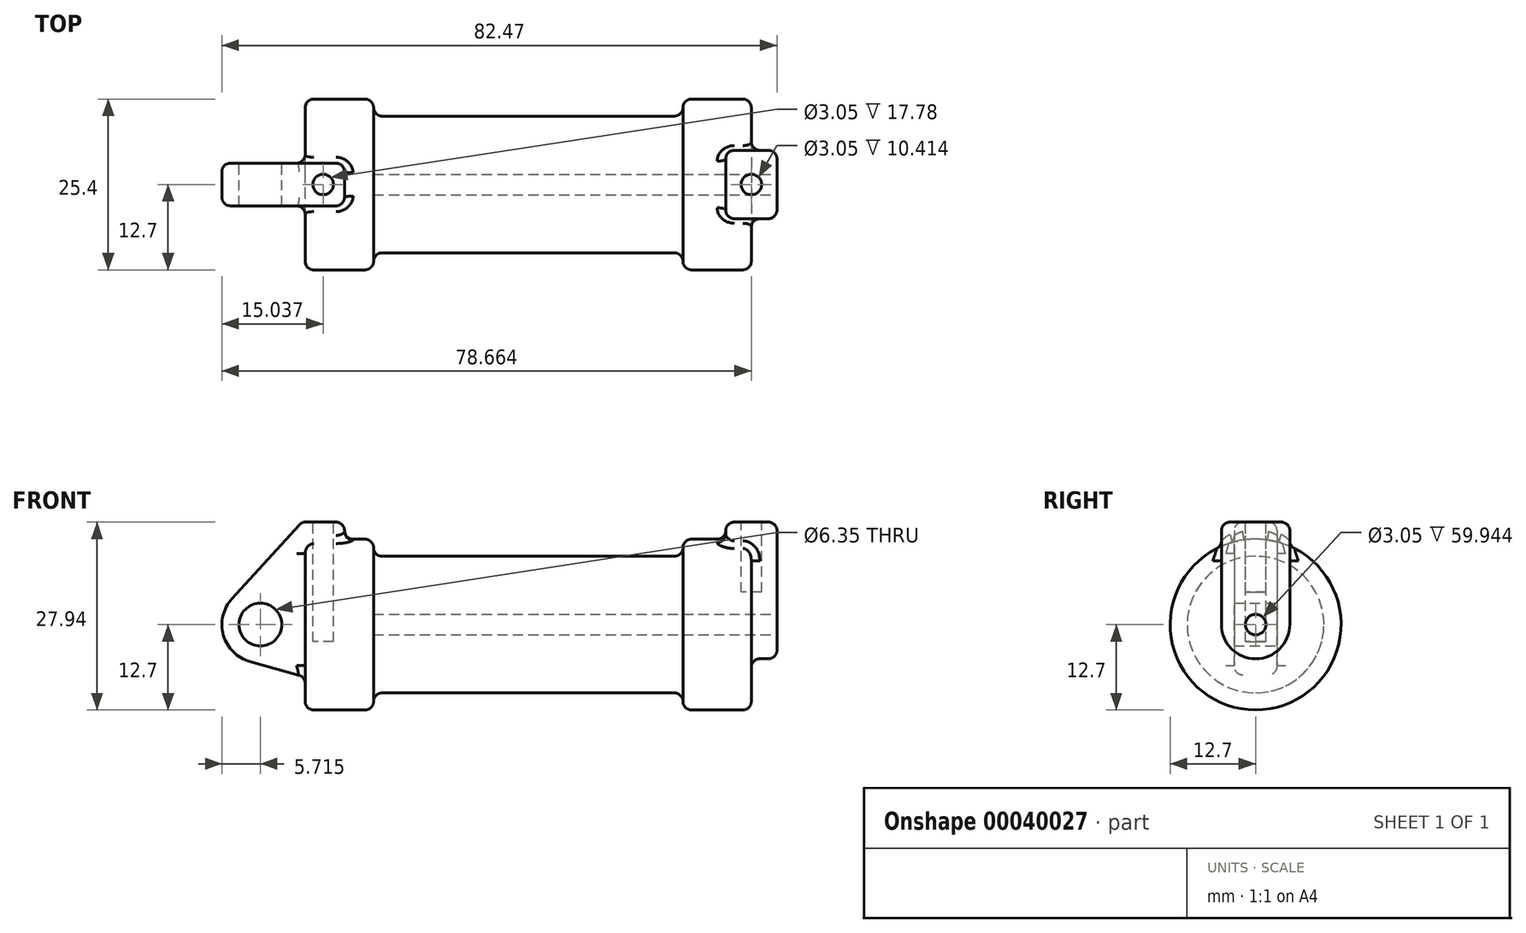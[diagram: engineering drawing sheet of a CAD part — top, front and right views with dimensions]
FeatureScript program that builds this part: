
annotation { "Feature Type Name" : "Feature", "Feature Type Description" : "" }
export const myFeature = defineFeature(function(context is Context, id is Id, definition is map)
    precondition{}
    {
        {
            var Q0;
            Q0=qCreatedBy(makeId("Front.planeOp"),FACE);
            var sketch = newSketch(context, id + "F0", { "sketchPlane" : qUnion([Q0])});
            skLineSegment(sketch, "E0", {"start": v(0, 0) * mm, "end": v(0, 12.7) * mm});
            skLineSegment(sketch, "E1", {"start": v(0, 12.7) * mm, "end": v(10.16, 12.7) * mm});
            skLineSegment(sketch, "E2", {"start": v(10.16, 12.7) * mm, "end": v(10.16, 10.16) * mm});
            skLineSegment(sketch, "E3", {"start": v(10.16, 10.16) * mm, "end": v(56.13, 10.16) * mm});
            skLineSegment(sketch, "E4", {"start": v(56.13, 10.16) * mm, "end": v(56.13, 12.7) * mm});
            skLineSegment(sketch, "E5", {"start": v(56.13, 12.7) * mm, "end": v(66.3, 12.7) * mm});
            skLineSegment(sketch, "E6", {"start": v(66.3, 12.7) * mm, "end": v(66.3, 0) * mm});
            skLineSegment(sketch, "E7", {"start": v(66.3, 0) * mm, "end": v(0, 0) * mm});
            skLineSegment(sketch, "E8", {"start": v(5.84, 15.24) * mm, "end": v(-0.5, 15.24) * mm});
            skLineSegment(sketch, "E9", {"start": v(-0.5, 15.24) * mm, "end": v(-10.88, 3.85) * mm});
            skLineSegment(sketch, "E10", {"start": v(0, 0) * mm, "end": v(-6.65, 0) * mm});
            skCircle(sketch, "E11", {"center": v(-6.65, 0) * mm, "radius": 5.72 * mm});
            skCircle(sketch, "E12", {"center": v(-6.65, 0) * mm, "radius": 3.18 * mm});
            skLineSegment(sketch, "E13", {"start": v(5.84, 15.24) * mm, "end": v(5.84, -9.4) * mm});
            skLineSegment(sketch, "E14", {"start": v(5.84, -9.4) * mm, "end": v(-8.18, -5.5) * mm});
            skSolve(sketch);
        }
        {
            var Q0;
            {var subQ6=sQuery(id+"F0.wireOp",EDGE,"E2");Q0=makeQuery(id+"F0.imprint","IMPRINT",FACE,{"disambiguationData":[TD([[makeQuery(id+"F0.imprint","IMPRINT",EDGE,{"derivedFrom":subQ6}),-1.0]])]});}
            var Q1;
            {var subQ5=sQuery(id+"F0.wireOp",EDGE,"E0");Q1=makeQuery(id+"F0.imprint","IMPRINT",FACE,{"disambiguationData":[TD([[makeQuery(id+"F0.imprint","IMPRINT",EDGE,{"derivedFrom":subQ5}),-1.0]])]});}
            var Q2;
            Q2=sQuery(id+"F0.wireOp",EDGE,"E7");
            revolve(context, id + "F1", {"entities" : qUnion([Q0, Q1]), "axis" : qUnion([Q2]), "revolveType" : RevolveType.FULL});
        }
        {
            var Q0;
            {var subQ5=sQuery(id+"F0.wireOp",EDGE,"E0");Q0=makeQuery(id+"F0.imprint","IMPRINT",FACE,{"disambiguationData":[TD([[makeQuery(id+"F0.imprint","IMPRINT",EDGE,{"derivedFrom":subQ5}),-1.0]])]});}
            var Q1;
            {var subQ8=sQuery(id+"F0.wireOp",EDGE,"E0");Q1=makeQuery(id+"F0.imprint","IMPRINT",FACE,{"disambiguationData":[TD([[makeQuery(id+"F0.imprint","IMPRINT",EDGE,{"derivedFrom":subQ8}),1.0]])]});}
            var Q2;
            {var subQ0=sQuery(id+"F0.wireOp",EDGE,"E12");Q2=makeQuery(id+"F0.imprint","IMPRINT",FACE,{"disambiguationData":[TD([[makeQuery(id+"F0.imprint","IMPRINT",EDGE,{"derivedFrom":subQ0}),-1.0]])]});}
            var Q3;
            {var subQ0=sQuery(id+"F0.wireOp",EDGE,"E14");Q3=makeQuery(id+"F0.imprint","IMPRINT",FACE,{"disambiguationData":[TD([[makeQuery(id+"F0.imprint","IMPRINT",EDGE,{"derivedFrom":subQ0}),-1.0]])]});}
            extrude(context, id + "F2", {"entities" : qUnion([Q0, Q1, Q2, Q3]), "operationType" : NewBodyOperationType.ADD, "endBound" : BoundingType.SYMMETRIC, "depth" : 6.35 * mm});
        }
        {
            var Q0;
            Q0=makeQuery(id+"F1.opRevolve","SWEPT_FACE",FACE,{"disambiguationData":[OSD([sQuery(id+"F0.wireOp",EDGE,"E6")])]});
            var sketch = newSketch(context, id + "F3", { "sketchPlane" : qUnion([Q0])});
            skCircle(sketch, "E15", {"center": v(0, 0) * mm, "radius": 1.52 * mm});
            skCircle(sketch, "E16", {"center": v(0, 0) * mm, "radius": 5.08 * mm});
            skLineSegment(sketch, "E17", {"start": v(5.08, 0) * mm, "end": v(5.08, 15.24) * mm});
            skLineSegment(sketch, "E18", {"start": v(5.08, 15.24) * mm, "end": v(-5.08, 15.24) * mm});
            skLineSegment(sketch, "E19", {"start": v(-5.08, 15.24) * mm, "end": v(-5.08, 0) * mm});
            skSolve(sketch);
        }
        {
            var Q0;
            Q0=makeQuery(id+"F3.imprint","IMPRINT",FACE,{"disambiguationData":[TD([[makeQuery(id+"F3.imprint","IMPRINT",EDGE,{"derivedFrom":sQuery(id+"F3.wireOp",EDGE,"E15")}),1.0]])]});
            var Q1;
            Q1=makeQuery(id+"F1.opRevolve","SWEPT_FACE",FACE,{"disambiguationData":[OSD([sQuery(id+"F0.wireOp",EDGE,"E2")])]});
            extrude(context, id + "F4", {"entities" : qUnion([Q0]), "operationType" : NewBodyOperationType.REMOVE, "endBound" : BoundingType.UP_TO_SURFACE, "oppositeDirection" : true, "endBoundEntityFace" : qUnion([Q1]), "depth" : 25.4 * mm});
        }
        {
            var Q0;
            Q0 = qSketchRegion(id + "F3", true);
            extrude(context, id + "F5", {"entities" : qUnion([Q0]), "operationType" : NewBodyOperationType.ADD, "endBound" : BoundingType.SYMMETRIC, "depth" : 7.62 * mm});
        }
        {
            var Q0;
            Q0=makeQuery(id+"F2.opExtrude","SWEPT_FACE",FACE,{"disambiguationData":[OSD([sQuery(id+"F0.wireOp",EDGE,"E8")])]});
            var sketch = newSketch(context, id + "F6", { "sketchPlane" : qUnion([Q0])});
            skCircle(sketch, "E20", {"center": v(2.67, 0) * mm, "radius": 1.52 * mm});
            skPoint(sketch, "E21", {"position": v(2.67, 3.18) * mm});
            skPoint(sketch, "E22", {"position": v(5.84, 0) * mm});
            skSolve(sketch);
        }
        {
            var Q0;
            Q0 = qSketchRegion(id + "F6", true);
            extrude(context, id + "F7", {"entities" : qUnion([Q0]), "operationType" : NewBodyOperationType.REMOVE, "oppositeDirection" : true, "depth" : 17.78 * mm});
        }
        {
            var Q0;
            Q0=makeQuery(id+"F5.opExtrude","SWEPT_FACE",FACE,{"disambiguationData":[OSD([sQuery(id+"F3.wireOp",EDGE,"E18")])]});
            var sketch = newSketch(context, id + "F8", { "sketchPlane" : qUnion([Q0])});
            skCircle(sketch, "E23", {"center": v(66.3, 0) * mm, "radius": 1.52 * mm});
            skPoint(sketch, "E23.centerSnap0", {"position": v(62.48, 0) * mm});
            skPoint(sketch, "E23.centerSnap1", {"position": v(66.3, 5.08) * mm});
            skSolve(sketch);
        }
        {
            var Q0;
            Q0 = qSketchRegion(id + "F8", true);
            extrude(context, id + "F9", {"entities" : qUnion([Q0]), "operationType" : NewBodyOperationType.REMOVE, "oppositeDirection" : true, "depth" : 10.4 * mm});
        }
        {
            var Q0;
            Q0=makeQuery(id+"F1.opRevolve","SWEPT_EDGE",EDGE,{"disambiguationData":[OSD([sQuery(id+"F0.wireOp",EDGE,"E1"),sQuery(id+"F0.wireOp",EDGE,"E2")])]});
            var Q1;
            Q1=makeQuery(id+"F1.opRevolve","SWEPT_EDGE",EDGE,{"disambiguationData":[OSD([sQuery(id+"F0.wireOp",EDGE,"E2"),sQuery(id+"F0.wireOp",EDGE,"E3")])]});
            var Q2;
            Q2=makeQuery(id+"F1.opRevolve","SWEPT_EDGE",EDGE,{"disambiguationData":[OSD([sQuery(id+"F0.wireOp",EDGE,"E3"),sQuery(id+"F0.wireOp",EDGE,"E4")])]});
            var Q3;
            Q3=makeQuery(id+"F1.opRevolve","SWEPT_EDGE",EDGE,{"disambiguationData":[OSD([sQuery(id+"F0.wireOp",EDGE,"E4"),sQuery(id+"F0.wireOp",EDGE,"E5")])]});
            var Q4;
            Q4=makeQuery(id+"F1.opRevolve","SWEPT_EDGE",EDGE,{"disambiguationData":[OSD([sQuery(id+"F0.wireOp",EDGE,"E5"),sQuery(id+"F0.wireOp",EDGE,"E6")])]});
            var Q5;
            Q5=makeQuery(id+"F1.opRevolve","SWEPT_EDGE",EDGE,{"disambiguationData":[OSD([sQuery(id+"F0.wireOp",EDGE,"E0"),sQuery(id+"F0.wireOp",EDGE,"E1")])]});
            fillet(context, id + "F10", {"entities" : qUnion([Q0, Q1, Q2, Q3, Q4, Q5]), "radius" : 1.27 * mm, "tangentPropagation" : true, "allowEdgeOverflow" : false});
        }
        {
            var Q0;
            Q0=makeQuery(id+"F2.boolean.opBoolean","INTERSECT",EDGE,{"derivedFrom":[makeQuery(id+"F1.opRevolve","SWEPT_FACE",FACE,{"disambiguationData":[OSD([sQuery(id+"F0.wireOp",EDGE,"E1")])]}),makeQuery(id+"F2.opExtrude","CAP_FACE",FACE,{"disambiguationData":[OSD([sQuery(id+"F0.wireOp",EDGE,"E8"),sQuery(id+"F0.wireOp",EDGE,"E9"),sQuery(id+"F0.wireOp",EDGE,"E11"),sQuery(id+"F0.wireOp",EDGE,"E12"),sQuery(id+"F0.wireOp",EDGE,"E13"),sQuery(id+"F0.wireOp",EDGE,"E14")])],"isStart":true})]});
            var Q1;
            Q1=makeQuery(id+"F10.opFillet","BLEND_EDGE",EDGE,{"blendedFrom":[makeQuery(id+"F1.opRevolve","SWEPT_EDGE",EDGE,{"disambiguationData":[OSD([sQuery(id+"F0.wireOp",EDGE,"E0"),sQuery(id+"F0.wireOp",EDGE,"E1")])]}),makeQuery(id+"F2.opExtrude","CAP_FACE",FACE,{"disambiguationData":[OSD([sQuery(id+"F0.wireOp",EDGE,"E8"),sQuery(id+"F0.wireOp",EDGE,"E9"),sQuery(id+"F0.wireOp",EDGE,"E11"),sQuery(id+"F0.wireOp",EDGE,"E12"),sQuery(id+"F0.wireOp",EDGE,"E13"),sQuery(id+"F0.wireOp",EDGE,"E14")])],"isStart":true})],"blendedInto":[makeQuery(id+"F2.opExtrude","CAP_FACE",FACE,{"disambiguationData":[OSD([sQuery(id+"F0.wireOp",EDGE,"E8"),sQuery(id+"F0.wireOp",EDGE,"E9"),sQuery(id+"F0.wireOp",EDGE,"E11"),sQuery(id+"F0.wireOp",EDGE,"E12"),sQuery(id+"F0.wireOp",EDGE,"E13"),sQuery(id+"F0.wireOp",EDGE,"E14")])],"isStart":true})]});
            var Q2;
            Q2=makeQuery(id+"F2.boolean.opBoolean","INTERSECT",EDGE,{"derivedFrom":[makeQuery(id+"F1.opRevolve","SWEPT_FACE",FACE,{"disambiguationData":[OSD([sQuery(id+"F0.wireOp",EDGE,"E0")])]}),makeQuery(id+"F2.opExtrude","CAP_FACE",FACE,{"disambiguationData":[OSD([sQuery(id+"F0.wireOp",EDGE,"E8"),sQuery(id+"F0.wireOp",EDGE,"E9"),sQuery(id+"F0.wireOp",EDGE,"E11"),sQuery(id+"F0.wireOp",EDGE,"E12"),sQuery(id+"F0.wireOp",EDGE,"E13"),sQuery(id+"F0.wireOp",EDGE,"E14")])],"isStart":true})]});
            var Q3;
            Q3=makeQuery(id+"F2.opExtrude","CAP_EDGE",EDGE,{"disambiguationData":[OSD([sQuery(id+"F0.wireOp",EDGE,"E13")])],"isStart":true});
            var Q4;
            Q4=makeQuery(id+"F2.opExtrude","CAP_EDGE",EDGE,{"disambiguationData":[OSD([sQuery(id+"F0.wireOp",EDGE,"E8")])],"isStart":true});
            var Q5;
            Q5=makeQuery(id+"F2.opExtrude","CAP_EDGE",EDGE,{"disambiguationData":[OSD([sQuery(id+"F0.wireOp",EDGE,"E9")])],"isStart":true});
            var Q6;
            Q6=makeQuery(id+"F2.opExtrude","SWEPT_EDGE",EDGE,{"disambiguationData":[OSD([sQuery(id+"F0.wireOp",EDGE,"E8"),sQuery(id+"F0.wireOp",EDGE,"E9")])]});
            var Q7;
            Q7=makeQuery(id+"F2.opExtrude","CAP_EDGE",EDGE,{"disambiguationData":[OSD([sQuery(id+"F0.wireOp",EDGE,"E11")])],"isStart":true});
            var Q8;
            Q8=makeQuery(id+"F2.opExtrude","CAP_EDGE",EDGE,{"disambiguationData":[OSD([sQuery(id+"F0.wireOp",EDGE,"E14")])],"isStart":true});
            var Q9;
            Q9=makeQuery(id+"F2.opExtrude","SWEPT_EDGE",EDGE,{"disambiguationData":[OSD([sQuery(id+"F0.wireOp",EDGE,"E8"),sQuery(id+"F0.wireOp",EDGE,"E13")])]});
            var Q10;
            Q10=makeQuery(id+"F2.opExtrude","CAP_EDGE",EDGE,{"disambiguationData":[OSD([sQuery(id+"F0.wireOp",EDGE,"E8")])],"isStart":false});
            var Q11;
            Q11=makeQuery(id+"F2.boolean.opBoolean","INTERSECT",EDGE,{"derivedFrom":[makeQuery(id+"F1.opRevolve","SWEPT_FACE",FACE,{"disambiguationData":[OSD([sQuery(id+"F0.wireOp",EDGE,"E0")])]}),makeQuery(id+"F2.opExtrude","SWEPT_FACE",FACE,{"disambiguationData":[OSD([sQuery(id+"F0.wireOp",EDGE,"E14")])]})]});
            var Q12;
            Q12=makeQuery(id+"F2.boolean.opBoolean","INTERSECT",EDGE,{"derivedFrom":[makeQuery(id+"F1.opRevolve","SWEPT_FACE",FACE,{"disambiguationData":[OSD([sQuery(id+"F0.wireOp",EDGE,"E0")])]}),makeQuery(id+"F2.opExtrude","CAP_FACE",FACE,{"disambiguationData":[OSD([sQuery(id+"F0.wireOp",EDGE,"E8"),sQuery(id+"F0.wireOp",EDGE,"E9"),sQuery(id+"F0.wireOp",EDGE,"E11"),sQuery(id+"F0.wireOp",EDGE,"E12"),sQuery(id+"F0.wireOp",EDGE,"E13"),sQuery(id+"F0.wireOp",EDGE,"E14")])],"isStart":false})]});
            var Q13;
            Q13=makeQuery(id+"F2.opExtrude","CAP_EDGE",EDGE,{"disambiguationData":[OSD([sQuery(id+"F0.wireOp",EDGE,"E14")])],"isStart":false});
            var Q14;
            Q14=makeQuery(id+"F2.opExtrude","CAP_EDGE",EDGE,{"disambiguationData":[OSD([sQuery(id+"F0.wireOp",EDGE,"E11")])],"isStart":false});
            var Q15;
            Q15=makeQuery(id+"F10.opFillet","BLEND_EDGE",EDGE,{"blendedFrom":[makeQuery(id+"F1.opRevolve","SWEPT_EDGE",EDGE,{"disambiguationData":[OSD([sQuery(id+"F0.wireOp",EDGE,"E0"),sQuery(id+"F0.wireOp",EDGE,"E1")])]}),makeQuery(id+"F2.opExtrude","CAP_FACE",FACE,{"disambiguationData":[OSD([sQuery(id+"F0.wireOp",EDGE,"E8"),sQuery(id+"F0.wireOp",EDGE,"E9"),sQuery(id+"F0.wireOp",EDGE,"E11"),sQuery(id+"F0.wireOp",EDGE,"E12"),sQuery(id+"F0.wireOp",EDGE,"E13"),sQuery(id+"F0.wireOp",EDGE,"E14")])],"isStart":false})],"blendedInto":[makeQuery(id+"F2.opExtrude","CAP_FACE",FACE,{"disambiguationData":[OSD([sQuery(id+"F0.wireOp",EDGE,"E8"),sQuery(id+"F0.wireOp",EDGE,"E9"),sQuery(id+"F0.wireOp",EDGE,"E11"),sQuery(id+"F0.wireOp",EDGE,"E12"),sQuery(id+"F0.wireOp",EDGE,"E13"),sQuery(id+"F0.wireOp",EDGE,"E14")])],"isStart":false})]});
            var Q16;
            Q16=makeQuery(id+"F2.boolean.opBoolean","INTERSECT",EDGE,{"derivedFrom":[makeQuery(id+"F1.opRevolve","SWEPT_FACE",FACE,{"disambiguationData":[OSD([sQuery(id+"F0.wireOp",EDGE,"E1")])]}),makeQuery(id+"F2.opExtrude","CAP_FACE",FACE,{"disambiguationData":[OSD([sQuery(id+"F0.wireOp",EDGE,"E8"),sQuery(id+"F0.wireOp",EDGE,"E9"),sQuery(id+"F0.wireOp",EDGE,"E11"),sQuery(id+"F0.wireOp",EDGE,"E12"),sQuery(id+"F0.wireOp",EDGE,"E13"),sQuery(id+"F0.wireOp",EDGE,"E14")])],"isStart":false})]});
            var Q17;
            Q17=makeQuery(id+"F2.opExtrude","CAP_EDGE",EDGE,{"disambiguationData":[OSD([sQuery(id+"F0.wireOp",EDGE,"E9")])],"isStart":false});
            var Q18;
            Q18=makeQuery(id+"F2.boolean.opBoolean","INTERSECT",EDGE,{"derivedFrom":[makeQuery(id+"F1.opRevolve","SWEPT_FACE",FACE,{"disambiguationData":[OSD([sQuery(id+"F0.wireOp",EDGE,"E1")])]}),makeQuery(id+"F2.opExtrude","SWEPT_FACE",FACE,{"disambiguationData":[OSD([sQuery(id+"F0.wireOp",EDGE,"E13")])]})]});
            var Q19;
            Q19=makeQuery(id+"F2.opExtrude","CAP_EDGE",EDGE,{"disambiguationData":[OSD([sQuery(id+"F0.wireOp",EDGE,"E13")])],"isStart":false});
            fillet(context, id + "F11", {"entities" : qUnion([Q0, Q1, Q2, Q3, Q4, Q5, Q6, Q7, Q8, Q9, Q10, Q11, Q12, Q13, Q14, Q15, Q16, Q17, Q18, Q19]), "radius" : 1.27 * mm, "tangentPropagation" : true, "allowEdgeOverflow" : false});
        }
        {
            var Q0;
            Q0=makeQuery(id+"F5.opExtrude","CAP_EDGE",EDGE,{"disambiguationData":[OSD([sQuery(id+"F3.wireOp",EDGE,"E17")])],"isStart":true});
            var Q1;
            Q1=makeQuery(id+"F5.boolean.opBoolean","INTERSECT",EDGE,{"derivedFrom":[makeQuery(id+"F1.opRevolve","SWEPT_FACE",FACE,{"disambiguationData":[OSD([sQuery(id+"F0.wireOp",EDGE,"E5")])]}),makeQuery(id+"F5.opExtrude","CAP_FACE",FACE,{"disambiguationData":[OSD([sQuery(id+"F3.wireOp",EDGE,"E15"),sQuery(id+"F3.wireOp",EDGE,"E16"),sQuery(id+"F3.wireOp",EDGE,"E17"),sQuery(id+"F3.wireOp",EDGE,"E18"),sQuery(id+"F3.wireOp",EDGE,"E19")])],"isStart":true})]});
            var Q2;
            Q2=makeQuery(id+"F5.opExtrude","CAP_EDGE",EDGE,{"disambiguationData":[OSD([sQuery(id+"F3.wireOp",EDGE,"E19")])],"isStart":true});
            var Q3;
            Q3=makeQuery(id+"F5.opExtrude","CAP_EDGE",EDGE,{"disambiguationData":[OSD([sQuery(id+"F3.wireOp",EDGE,"E18")])],"isStart":true});
            var Q4;
            Q4=makeQuery(id+"F5.opExtrude","SWEPT_EDGE",EDGE,{"disambiguationData":[OSD([sQuery(id+"F3.wireOp",EDGE,"E18"),sQuery(id+"F3.wireOp",EDGE,"E19")])]});
            var Q5;
            Q5=makeQuery(id+"F5.opExtrude","CAP_EDGE",EDGE,{"disambiguationData":[OSD([sQuery(id+"F3.wireOp",EDGE,"E18")])],"isStart":false});
            var Q6;
            Q6=makeQuery(id+"F5.opExtrude","SWEPT_EDGE",EDGE,{"disambiguationData":[OSD([sQuery(id+"F3.wireOp",EDGE,"E17"),sQuery(id+"F3.wireOp",EDGE,"E18")])]});
            var Q7;
            Q7=makeQuery(id+"F5.boolean.opBoolean","INTERSECT",EDGE,{"derivedFrom":[makeQuery(id+"F1.opRevolve","SWEPT_FACE",FACE,{"disambiguationData":[OSD([sQuery(id+"F0.wireOp",EDGE,"E5")])]}),makeQuery(id+"F5.opExtrude","SWEPT_FACE",FACE,{"disambiguationData":[OSD([sQuery(id+"F3.wireOp",EDGE,"E17")])]})]});
            var Q8;
            Q8=makeQuery(id+"F10.opFillet","BLEND_EDGE",EDGE,{"blendedFrom":[makeQuery(id+"F1.opRevolve","SWEPT_EDGE",EDGE,{"disambiguationData":[OSD([sQuery(id+"F0.wireOp",EDGE,"E5"),sQuery(id+"F0.wireOp",EDGE,"E6")])]}),makeQuery(id+"F5.opExtrude","SWEPT_FACE",FACE,{"disambiguationData":[OSD([sQuery(id+"F3.wireOp",EDGE,"E19")])]})],"blendedInto":[makeQuery(id+"F5.opExtrude","SWEPT_FACE",FACE,{"disambiguationData":[OSD([sQuery(id+"F3.wireOp",EDGE,"E19")])]})]});
            var Q9;
            Q9=makeQuery(id+"F5.boolean.opBoolean","INTERSECT",EDGE,{"derivedFrom":[makeQuery(id+"F1.opRevolve","SWEPT_FACE",FACE,{"disambiguationData":[OSD([sQuery(id+"F0.wireOp",EDGE,"E6")])]}),makeQuery(id+"F5.opExtrude","SWEPT_FACE",FACE,{"disambiguationData":[OSD([sQuery(id+"F3.wireOp",EDGE,"E19")])]})]});
            var Q10;
            Q10=makeQuery(id+"F5.boolean.opBoolean","INTERSECT",EDGE,{"derivedFrom":[makeQuery(id+"F1.opRevolve","SWEPT_FACE",FACE,{"disambiguationData":[OSD([sQuery(id+"F0.wireOp",EDGE,"E6")])]}),makeQuery(id+"F5.opExtrude","SWEPT_FACE",FACE,{"disambiguationData":[OSD([sQuery(id+"F3.wireOp",EDGE,"E16")])]})]});
            var Q11;
            Q11=makeQuery(id+"F5.opExtrude","CAP_EDGE",EDGE,{"disambiguationData":[OSD([sQuery(id+"F3.wireOp",EDGE,"E16")])],"isStart":false});
            var Q12;
            Q12=makeQuery(id+"F5.opExtrude","CAP_EDGE",EDGE,{"disambiguationData":[OSD([sQuery(id+"F3.wireOp",EDGE,"E19")])],"isStart":false});
            var Q13;
            Q13=makeQuery(id+"F5.boolean.opBoolean","INTERSECT",EDGE,{"derivedFrom":[makeQuery(id+"F1.opRevolve","SWEPT_FACE",FACE,{"disambiguationData":[OSD([sQuery(id+"F0.wireOp",EDGE,"E5")])]}),makeQuery(id+"F5.opExtrude","SWEPT_FACE",FACE,{"disambiguationData":[OSD([sQuery(id+"F3.wireOp",EDGE,"E19")])]})]});
            var Q14;
            Q14=makeQuery(id+"F5.opExtrude","CAP_EDGE",EDGE,{"disambiguationData":[OSD([sQuery(id+"F3.wireOp",EDGE,"E17")])],"isStart":false});
            var Q15;
            Q15=makeQuery(id+"F5.boolean.opBoolean","INTERSECT",EDGE,{"derivedFrom":[makeQuery(id+"F1.opRevolve","SWEPT_FACE",FACE,{"disambiguationData":[OSD([sQuery(id+"F0.wireOp",EDGE,"E6")])]}),makeQuery(id+"F5.opExtrude","SWEPT_FACE",FACE,{"disambiguationData":[OSD([sQuery(id+"F3.wireOp",EDGE,"E17")])]})]});
            var Q16;
            Q16=makeQuery(id+"F10.opFillet","BLEND_EDGE",EDGE,{"blendedFrom":[makeQuery(id+"F1.opRevolve","SWEPT_EDGE",EDGE,{"disambiguationData":[OSD([sQuery(id+"F0.wireOp",EDGE,"E5"),sQuery(id+"F0.wireOp",EDGE,"E6")])]}),makeQuery(id+"F5.opExtrude","SWEPT_FACE",FACE,{"disambiguationData":[OSD([sQuery(id+"F3.wireOp",EDGE,"E17")])]})],"blendedInto":[makeQuery(id+"F5.opExtrude","SWEPT_FACE",FACE,{"disambiguationData":[OSD([sQuery(id+"F3.wireOp",EDGE,"E17")])]})]});
            fillet(context, id + "F12", {"entities" : qUnion([Q0, Q1, Q2, Q3, Q4, Q5, Q6, Q7, Q8, Q9, Q10, Q11, Q12, Q13, Q14, Q15, Q16]), "radius" : 1.27 * mm, "tangentPropagation" : true, "allowEdgeOverflow" : false});
        }
    });
